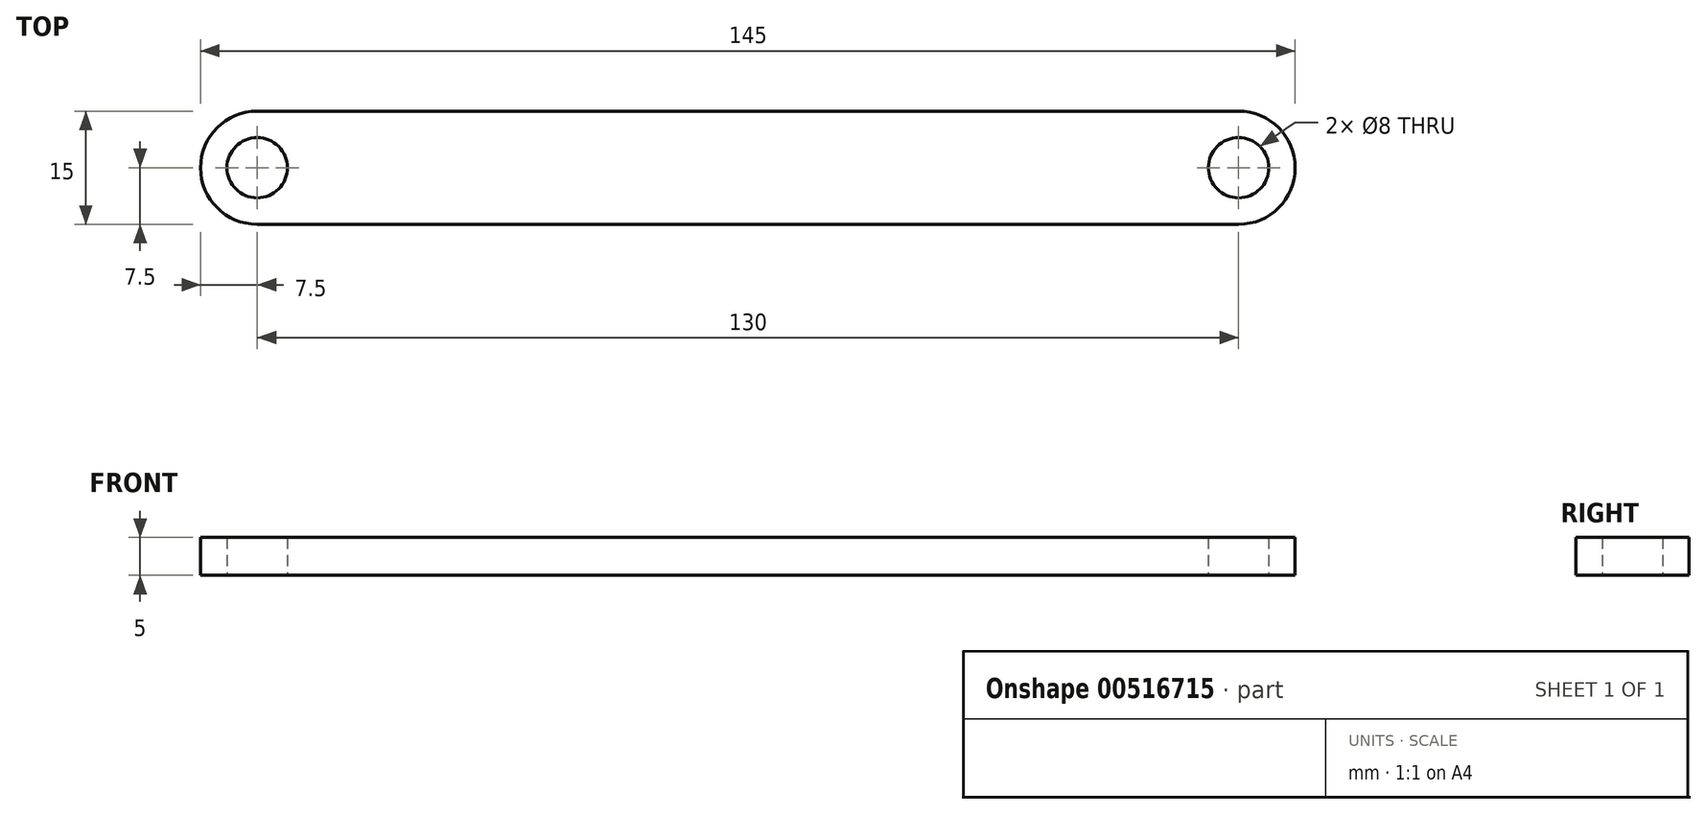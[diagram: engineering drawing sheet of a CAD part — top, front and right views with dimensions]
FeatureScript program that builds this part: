
annotation { "Feature Type Name" : "Feature", "Feature Type Description" : "" }
export const myFeature = defineFeature(function(context is Context, id is Id, definition is map)
    precondition{}
    {
        {
            var Q0;
            Q0=qCreatedBy(makeId("Top.planeOp"),FACE);
            var sketch = newSketch(context, id + "F0", { "sketchPlane" : qUnion([Q0])});
            skLineSegment(sketch, "E0.bottom", {"start": v(-65, 7.5) * mm, "end": v(65, 7.5) * mm});
            skLineSegment(sketch, "E0.top", {"start": v(-65, -7.5) * mm, "end": v(65, -7.5) * mm});
            skPoint(sketch, "E0.middle", {"position": v(0, 0) * mm});
            skArc(sketch, "E1", {"start": v(-65, 7.5) * mm, "mid": v(-72.5, 0) * mm, "end": v(-65, -7.5) * mm});
            skArc(sketch, "E2", {"start": v(65, -7.5) * mm, "mid": v(72.5, 0) * mm, "end": v(65, 7.5) * mm});
            skCircle(sketch, "E3", {"center": v(65, 0) * mm, "radius": 4 * mm});
            skCircle(sketch, "E4", {"center": v(-65, 0) * mm, "radius": 4 * mm});
            skSolve(sketch);
        }
        {
            var Q0;
            Q0=makeQuery(id+"F0.imprint","IMPRINT",FACE,{"disambiguationData":[TD([[makeQuery(id+"F0.imprint","IMPRINT",EDGE,{"derivedFrom":sQuery(id+"F0.wireOp",EDGE,"E0.bottom")}),-1.0]])]});
            extrude(context, id + "F1", {"entities" : qUnion([Q0]), "endBound" : BoundingType.SYMMETRIC, "depth" : 5 * mm, "offsetDistance" : 25.4 * mm});
        }
    });
